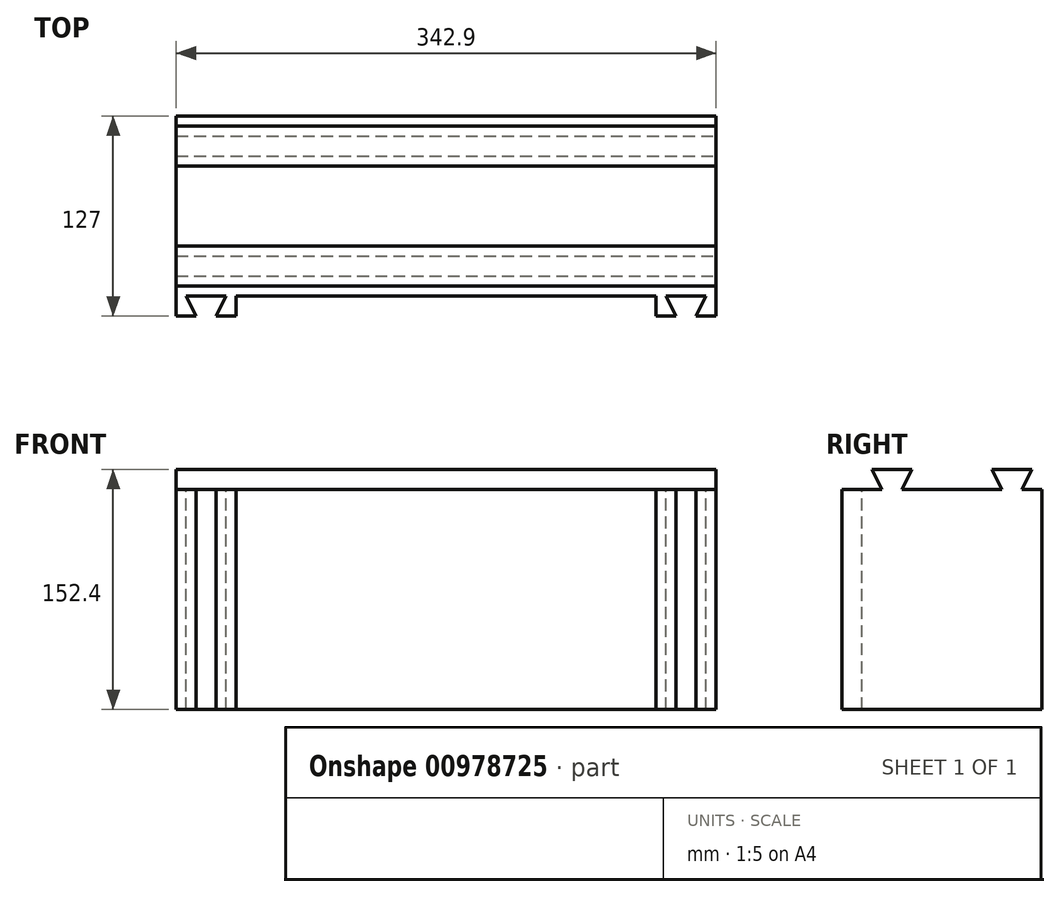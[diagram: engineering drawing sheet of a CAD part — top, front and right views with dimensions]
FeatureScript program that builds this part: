
annotation { "Feature Type Name" : "Feature", "Feature Type Description" : "" }
export const myFeature = defineFeature(function(context is Context, id is Id, definition is map)
    precondition{}
    {
        {
            var Q0;
            Q0=qCreatedBy(makeId("Top.planeOp"),FACE);
            var sketch = newSketch(context, id + "F0", { "sketchPlane" : qUnion([Q0])});
            skLineSegment(sketch, "E0.bottom", {"start": v(-177.8, 63.5) * mm, "end": v(177.8, 63.5) * mm});
            skLineSegment(sketch, "E0.top", {"start": v(-177.8, -63.5) * mm, "end": v(177.8, -63.5) * mm});
            skLineSegment(sketch, "E0.left", {"start": v(-177.8, 63.5) * mm, "end": v(-177.8, -63.5) * mm});
            skLineSegment(sketch, "E0.right", {"start": v(177.8, 63.5) * mm, "end": v(177.8, -63.5) * mm});
            skPoint(sketch, "E0.middle", {"position": v(0, 0) * mm});
            skSolve(sketch);
        }
        {
            var Q0;
            Q0=makeQuery(id+"F0.imprint","IMPRINT",FACE,{"disambiguationData":[TD([[makeQuery(id+"F0.imprint","IMPRINT",EDGE,{"derivedFrom":sQuery(id+"F0.wireOp",EDGE,"E0.bottom")}),-1.0]])]});
            extrude(context, id + "F1", {"entities" : qUnion([Q0]), "oppositeDirection" : true, "depth" : 152.4 * mm, "offsetDistance" : 25.4 * mm});
        }
        {
            var Q0;
            Q0=makeQuery(id+"F1.opExtrude","CAP_FACE",FACE,{"disambiguationData":[OSD([sQuery(id+"F0.wireOp",EDGE,"E0.bottom"),sQuery(id+"F0.wireOp",EDGE,"E0.top"),sQuery(id+"F0.wireOp",EDGE,"E0.left"),sQuery(id+"F0.wireOp",EDGE,"E0.right")])],"isStart":true});
            var sketch = newSketch(context, id + "F2", { "sketchPlane" : qUnion([Q0])});
            skLineSegment(sketch, "E1.bottom", {"start": v(177.8, -63.5) * mm, "end": v(139.7, -63.5) * mm});
            skLineSegment(sketch, "E1.top", {"start": v(177.8, -50.8) * mm, "end": v(139.7, -50.8) * mm});
            skLineSegment(sketch, "E1.left", {"start": v(177.8, -63.5) * mm, "end": v(177.8, -50.8) * mm});
            skLineSegment(sketch, "E1.right", {"start": v(139.7, -63.5) * mm, "end": v(139.7, -50.8) * mm});
            skLineSegment(sketch, "E2.bottom", {"start": v(-165.1, -63.5) * mm, "end": v(-127, -63.5) * mm});
            skLineSegment(sketch, "E2.top", {"start": v(-165.1, -50.8) * mm, "end": v(-127, -50.8) * mm});
            skLineSegment(sketch, "E2.left", {"start": v(-165.1, -63.5) * mm, "end": v(-165.1, -50.8) * mm});
            skLineSegment(sketch, "E2.right", {"start": v(-127, -63.5) * mm, "end": v(-127, -50.8) * mm});
            skLineSegment(sketch, "E3", {"start": v(-152.4, -63.5) * mm, "end": v(-158.75, -50.8) * mm});
            skLineSegment(sketch, "E4", {"start": v(-158.75, -50.8) * mm, "end": v(-158.75, -63.5) * mm});
            skLineSegment(sketch, "E5", {"start": v(-139.7, -63.5) * mm, "end": v(-133.35, -50.8) * mm});
            skLineSegment(sketch, "E6", {"start": v(-133.35, -50.8) * mm, "end": v(-133.35, -63.5) * mm});
            skLineSegment(sketch, "E7", {"start": v(152.4, -63.5) * mm, "end": v(146.05, -50.8) * mm});
            skLineSegment(sketch, "E8", {"start": v(146.05, -50.8) * mm, "end": v(146.05, -63.5) * mm});
            skLineSegment(sketch, "E9", {"start": v(165.1, -63.5) * mm, "end": v(171.45, -50.8) * mm});
            skLineSegment(sketch, "E10", {"start": v(171.45, -50.8) * mm, "end": v(171.45, -63.5) * mm});
            skLineSegment(sketch, "E11", {"start": v(139.7, -50.8) * mm, "end": v(-127, -50.8) * mm});
            skSolve(sketch);
        }
        {
            var Q0;
            {var subQ0=sQuery(id+"F2.wireOp",EDGE,"E7");Q0=makeQuery(id+"F2.imprint","IMPRINT",FACE,{"disambiguationData":[TD([[makeQuery(id+"F2.imprint","IMPRINT",EDGE,{"derivedFrom":subQ0}),-1.0]])]});}
            var Q1;
            {var subQ0=sQuery(id+"F2.wireOp",EDGE,"E1.right");Q1=makeQuery(id+"F2.imprint","IMPRINT",FACE,{"disambiguationData":[TD([[makeQuery(id+"F2.imprint","IMPRINT",EDGE,{"derivedFrom":subQ0}),1.0]])]});}
            var Q2;
            {var subQ0=sQuery(id+"F2.wireOp",EDGE,"E3");Q2=makeQuery(id+"F2.imprint","IMPRINT",FACE,{"disambiguationData":[TD([[makeQuery(id+"F2.imprint","IMPRINT",EDGE,{"derivedFrom":subQ0}),-1.0]])]});}
            extrude(context, id + "F3", {"entities" : qUnion([Q0, Q1, Q2]), "operationType" : NewBodyOperationType.REMOVE, "oppositeDirection" : true, "depth" : 152.4 * mm, "offsetDistance" : 25.4 * mm});
        }
        {
            var Q0;
            Q0=makeQuery(id+"F1.opExtrude","CAP_FACE",FACE,{"disambiguationData":[OSD([sQuery(id+"F0.wireOp",EDGE,"E0.bottom"),sQuery(id+"F0.wireOp",EDGE,"E0.top"),sQuery(id+"F0.wireOp",EDGE,"E0.left"),sQuery(id+"F0.wireOp",EDGE,"E0.right")])],"isStart":true});
            var sketch = newSketch(context, id + "F4", { "sketchPlane" : qUnion([Q0])});
            skLineSegment(sketch, "E12.bottom", {"start": v(-177.8, 63.5) * mm, "end": v(-165.1, 63.5) * mm});
            skLineSegment(sketch, "E12.top", {"start": v(-177.8, 25.4) * mm, "end": v(-165.1, 25.4) * mm});
            skLineSegment(sketch, "E12.left", {"start": v(-177.8, 63.5) * mm, "end": v(-177.8, 25.4) * mm});
            skLineSegment(sketch, "E12.right", {"start": v(-165.1, 63.5) * mm, "end": v(-165.1, 25.4) * mm});
            skLineSegment(sketch, "E13.bottom", {"start": v(-177.8, -63.5) * mm, "end": v(-165.1, -63.5) * mm});
            skLineSegment(sketch, "E13.top", {"start": v(-177.8, -12.7) * mm, "end": v(-165.1, -12.7) * mm});
            skLineSegment(sketch, "E13.left", {"start": v(-177.8, -63.5) * mm, "end": v(-177.8, -12.7) * mm});
            skLineSegment(sketch, "E13.right", {"start": v(-165.1, -63.5) * mm, "end": v(-165.1, -12.7) * mm});
            skLineSegment(sketch, "E14", {"start": v(-177.8, 50.8) * mm, "end": v(-165.1, 57.15) * mm});
            skLineSegment(sketch, "E15", {"start": v(-165.1, 57.15) * mm, "end": v(-177.8, 57.15) * mm});
            skLineSegment(sketch, "E16", {"start": v(-177.8, 38.1) * mm, "end": v(-165.1, 31.75) * mm});
            skLineSegment(sketch, "E17", {"start": v(-165.1, 31.75) * mm, "end": v(-177.8, 31.75) * mm});
            skLineSegment(sketch, "E18", {"start": v(-177.8, -25.4) * mm, "end": v(-165.1, -19.05) * mm});
            skLineSegment(sketch, "E19", {"start": v(-165.1, -19.05) * mm, "end": v(-177.8, -19.05) * mm});
            skLineSegment(sketch, "E20", {"start": v(-165.1, -50.8) * mm, "end": v(-177.8, -50.8) * mm});
            skLineSegment(sketch, "E21", {"start": v(-165.1, -44.45) * mm, "end": v(-177.8, -44.45) * mm});
            skLineSegment(sketch, "E22", {"start": v(-165.1, -44.45) * mm, "end": v(-177.8, -38.1) * mm});
            skLineSegment(sketch, "E23", {"start": v(-165.1, 25.4) * mm, "end": v(-165.1, -12.7) * mm});
            skSolve(sketch);
        }
        {
            var Q0;
            {var subQ0=sQuery(id+"F4.wireOp",EDGE,"E13.bottom");Q0=makeQuery(id+"F4.imprint","IMPRINT",FACE,{"disambiguationData":[TD([[makeQuery(id+"F4.imprint","IMPRINT",EDGE,{"derivedFrom":subQ0}),1.0]])]});}
            var Q1;
            {var subQ0=sQuery(id+"F4.wireOp",EDGE,"E14");Q1=makeQuery(id+"F4.imprint","IMPRINT",FACE,{"disambiguationData":[TD([[makeQuery(id+"F4.imprint","IMPRINT",EDGE,{"derivedFrom":subQ0}),1.0]])]});}
            var Q2;
            {var subQ0=sQuery(id+"F4.wireOp",EDGE,"E12.bottom");Q2=makeQuery(id+"F4.imprint","IMPRINT",FACE,{"disambiguationData":[TD([[makeQuery(id+"F4.imprint","IMPRINT",EDGE,{"derivedFrom":subQ0}),-1.0]])]});}
            var Q3;
            {var subQ0=sQuery(id+"F4.wireOp",EDGE,"E16");Q3=makeQuery(id+"F4.imprint","IMPRINT",FACE,{"disambiguationData":[TD([[makeQuery(id+"F4.imprint","IMPRINT",EDGE,{"derivedFrom":subQ0}),-1.0]])]});}
            var Q4;
            {var subQ0=sQuery(id+"F4.wireOp",EDGE,"E12.top");Q4=makeQuery(id+"F4.imprint","IMPRINT",FACE,{"disambiguationData":[TD([[makeQuery(id+"F4.imprint","IMPRINT",EDGE,{"derivedFrom":subQ0}),1.0]])]});}
            var Q5;
            {var subQ0=sQuery(id+"F4.wireOp",EDGE,"E13.top");Q5=makeQuery(id+"F4.imprint","IMPRINT",FACE,{"disambiguationData":[TD([[makeQuery(id+"F4.imprint","IMPRINT",EDGE,{"derivedFrom":subQ0}),-1.0]])]});}
            var Q6;
            {var subQ0=sQuery(id+"F4.wireOp",EDGE,"E18");Q6=makeQuery(id+"F4.imprint","IMPRINT",FACE,{"disambiguationData":[TD([[makeQuery(id+"F4.imprint","IMPRINT",EDGE,{"derivedFrom":subQ0}),1.0]])]});}
            var Q7;
            {var subQ0=sQuery(id+"F4.wireOp",EDGE,"E21");Q7=makeQuery(id+"F4.imprint","IMPRINT",FACE,{"disambiguationData":[TD([[makeQuery(id+"F4.imprint","IMPRINT",EDGE,{"derivedFrom":subQ0}),-1.0]])]});}
            var Q8;
            {var subQ0=sQuery(id+"F4.wireOp",EDGE,"E20");Q8=makeQuery(id+"F4.imprint","IMPRINT",FACE,{"disambiguationData":[TD([[makeQuery(id+"F4.imprint","IMPRINT",EDGE,{"derivedFrom":subQ0}),-1.0]])]});}
            var Q9;
            {var subQ0=sQuery(id+"F4.wireOp",EDGE,"E12.top");Q9=makeQuery(id+"F4.imprint","IMPRINT",FACE,{"disambiguationData":[TD([[makeQuery(id+"F4.imprint","IMPRINT",EDGE,{"derivedFrom":subQ0}),-1.0]])]});}
            var Q10;
            {var subQ0=sQuery(id+"F4.wireOp",EDGE,"E18");Q10=makeQuery(id+"F4.imprint","IMPRINT",FACE,{"disambiguationData":[TD([[makeQuery(id+"F4.imprint","IMPRINT",EDGE,{"derivedFrom":subQ0}),-1.0]])]});}
            var Q11;
            {var subQ0=sQuery(id+"F4.wireOp",EDGE,"E14");Q11=makeQuery(id+"F4.imprint","IMPRINT",FACE,{"disambiguationData":[TD([[makeQuery(id+"F4.imprint","IMPRINT",EDGE,{"derivedFrom":subQ0}),-1.0]])]});}
            extrude(context, id + "F5", {"entities" : qUnion([Q0, Q1, Q2, Q3, Q4, Q5, Q6, Q7, Q8, Q9, Q10, Q11]), "operationType" : NewBodyOperationType.REMOVE, "oppositeDirection" : true, "depth" : 152.4 * mm, "offsetDistance" : 25.4 * mm});
        }
        {
            var Q0;
            Q0=makeQuery(id+"F1.opExtrude","SWEPT_FACE",FACE,{"disambiguationData":[OSD([sQuery(id+"F0.wireOp",EDGE,"E0.right")])]});
            var sketch = newSketch(context, id + "F6", { "sketchPlane" : qUnion([Q0])});
            skLineSegment(sketch, "E24.bottom", {"start": v(-50.8, 0) * mm, "end": v(-12.7, 0) * mm});
            skLineSegment(sketch, "E24.top", {"start": v(-50.8, -12.7) * mm, "end": v(-12.7, -12.7) * mm});
            skLineSegment(sketch, "E24.left", {"start": v(-50.8, 0) * mm, "end": v(-50.8, -12.7) * mm});
            skLineSegment(sketch, "E24.right", {"start": v(-12.7, 0) * mm, "end": v(-12.7, -12.7) * mm});
            skLineSegment(sketch, "E25.bottom", {"start": v(63.5, 0) * mm, "end": v(25.4, 0) * mm});
            skLineSegment(sketch, "E25.top", {"start": v(63.5, -12.7) * mm, "end": v(25.4, -12.7) * mm});
            skLineSegment(sketch, "E25.left", {"start": v(63.5, 0) * mm, "end": v(63.5, -12.7) * mm});
            skLineSegment(sketch, "E25.right", {"start": v(25.4, 0) * mm, "end": v(25.4, -12.7) * mm});
            skLineSegment(sketch, "E26", {"start": v(-44.45, 0) * mm, "end": v(-44.45, -12.7) * mm});
            skLineSegment(sketch, "E27", {"start": v(-19.05, 0) * mm, "end": v(-19.05, -12.7) * mm});
            skLineSegment(sketch, "E28", {"start": v(31.75, 0) * mm, "end": v(31.75, -12.7) * mm});
            skLineSegment(sketch, "E29", {"start": v(57.15, 0) * mm, "end": v(57.15, -12.7) * mm});
            skLineSegment(sketch, "E30", {"start": v(-50.8, -12.7) * mm, "end": v(-63.5, -12.7) * mm});
            skLineSegment(sketch, "E31", {"start": v(-12.7, -12.7) * mm, "end": v(25.4, -12.7) * mm});
            skLineSegment(sketch, "E32", {"start": v(57.15, 0) * mm, "end": v(50.8, -12.7) * mm});
            skLineSegment(sketch, "E33", {"start": v(31.75, 0) * mm, "end": v(38.1, -12.7) * mm});
            skLineSegment(sketch, "E34", {"start": v(-19.05, 0) * mm, "end": v(-25.4, -12.7) * mm});
            skLineSegment(sketch, "E35", {"start": v(-44.45, 0) * mm, "end": v(-38.1, -12.7) * mm});
            skSolve(sketch);
        }
        {
            var Q0;
            {var subQ0=sQuery(id+"F6.wireOp",EDGE,"E24.left");Q0=makeQuery(id+"F6.imprint","IMPRINT",FACE,{"disambiguationData":[TD([[makeQuery(id+"F6.imprint","IMPRINT",EDGE,{"derivedFrom":subQ0}),-1.0]])]});}
            var Q1;
            {var subQ0=sQuery(id+"F6.wireOp",EDGE,"E24.left");Q1=makeQuery(id+"F6.imprint","IMPRINT",FACE,{"disambiguationData":[TD([[makeQuery(id+"F6.imprint","IMPRINT",EDGE,{"derivedFrom":subQ0}),1.0]])]});}
            var Q2;
            {var subQ0=sQuery(id+"F6.wireOp",EDGE,"E26");Q2=makeQuery(id+"F6.imprint","IMPRINT",FACE,{"disambiguationData":[TD([[makeQuery(id+"F6.imprint","IMPRINT",EDGE,{"derivedFrom":subQ0}),1.0]])]});}
            var Q3;
            {var subQ0=sQuery(id+"F6.wireOp",EDGE,"E27");Q3=makeQuery(id+"F6.imprint","IMPRINT",FACE,{"disambiguationData":[TD([[makeQuery(id+"F6.imprint","IMPRINT",EDGE,{"derivedFrom":subQ0}),-1.0]])]});}
            var Q4;
            {var subQ0=sQuery(id+"F6.wireOp",EDGE,"E24.right");Q4=makeQuery(id+"F6.imprint","IMPRINT",FACE,{"disambiguationData":[TD([[makeQuery(id+"F6.imprint","IMPRINT",EDGE,{"derivedFrom":subQ0}),-1.0]])]});}
            var Q5;
            {var subQ0=sQuery(id+"F6.wireOp",EDGE,"E24.right");Q5=makeQuery(id+"F6.imprint","IMPRINT",FACE,{"disambiguationData":[TD([[makeQuery(id+"F6.imprint","IMPRINT",EDGE,{"derivedFrom":subQ0}),1.0]])]});}
            var Q6;
            {var subQ0=sQuery(id+"F6.wireOp",EDGE,"E25.right");Q6=makeQuery(id+"F6.imprint","IMPRINT",FACE,{"disambiguationData":[TD([[makeQuery(id+"F6.imprint","IMPRINT",EDGE,{"derivedFrom":subQ0}),1.0]])]});}
            var Q7;
            {var subQ0=sQuery(id+"F6.wireOp",EDGE,"E28");Q7=makeQuery(id+"F6.imprint","IMPRINT",FACE,{"disambiguationData":[TD([[makeQuery(id+"F6.imprint","IMPRINT",EDGE,{"derivedFrom":subQ0}),1.0]])]});}
            var Q8;
            {var subQ0=sQuery(id+"F6.wireOp",EDGE,"E29");Q8=makeQuery(id+"F6.imprint","IMPRINT",FACE,{"disambiguationData":[TD([[makeQuery(id+"F6.imprint","IMPRINT",EDGE,{"derivedFrom":subQ0}),-1.0]])]});}
            var Q9;
            {var subQ0=sQuery(id+"F6.wireOp",EDGE,"E25.left");Q9=makeQuery(id+"F6.imprint","IMPRINT",FACE,{"disambiguationData":[TD([[makeQuery(id+"F6.imprint","IMPRINT",EDGE,{"derivedFrom":subQ0}),1.0]])]});}
            extrude(context, id + "F7", {"entities" : qUnion([Q0, Q1, Q2, Q3, Q4, Q5, Q6, Q7, Q8, Q9]), "operationType" : NewBodyOperationType.REMOVE, "oppositeDirection" : true, "depth" : 342.9 * mm, "offsetDistance" : 25.4 * mm});
        }
    });
